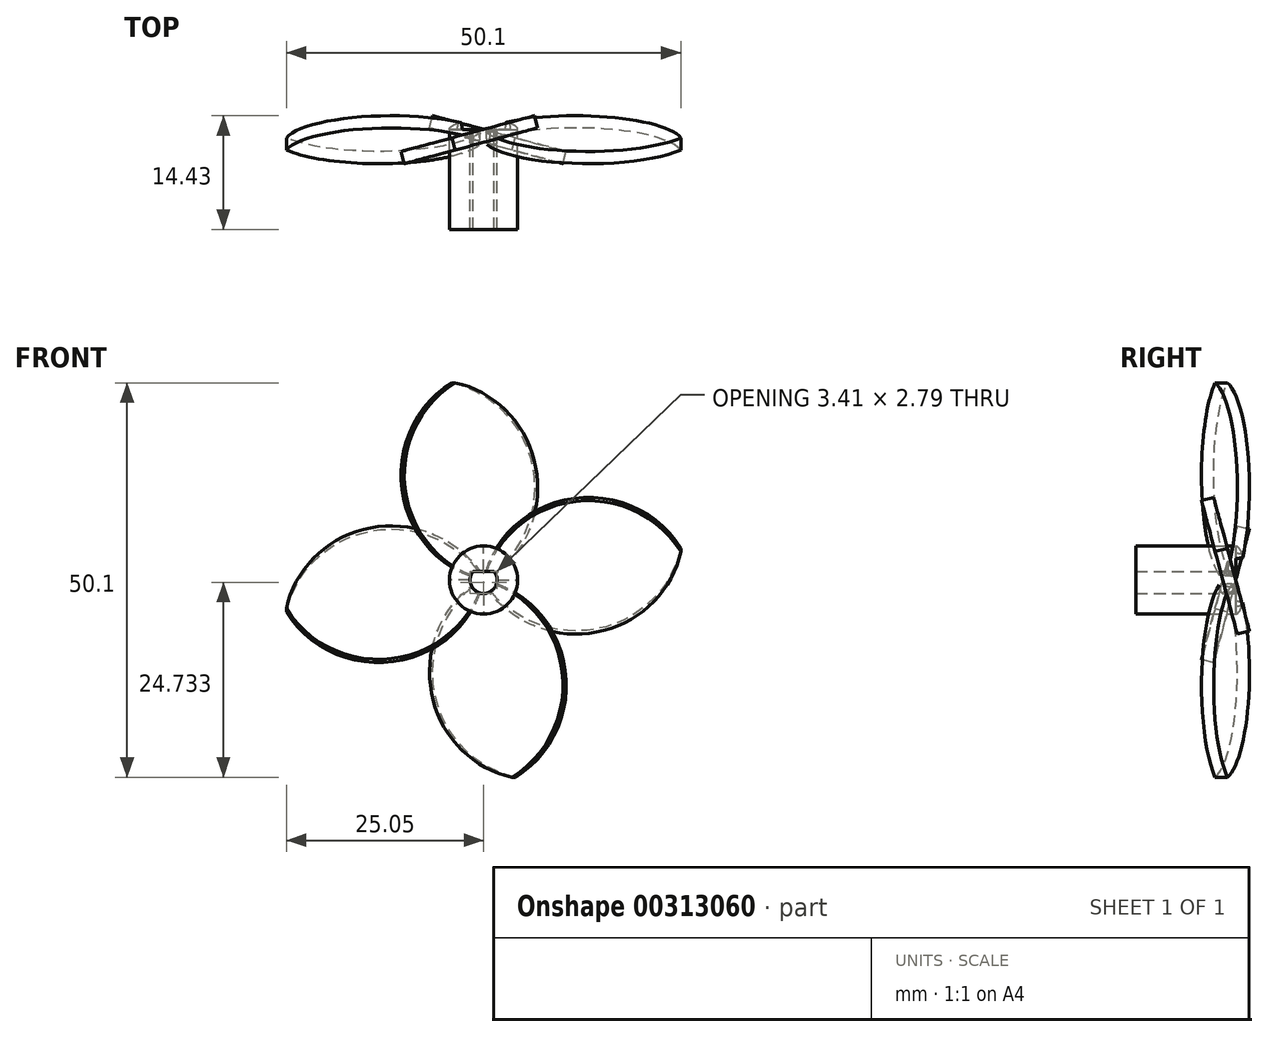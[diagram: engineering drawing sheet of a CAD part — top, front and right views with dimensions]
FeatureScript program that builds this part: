
annotation { "Feature Type Name" : "Feature", "Feature Type Description" : "" }
export const myFeature = defineFeature(function(context is Context, id is Id, definition is map)
    precondition{}
    {
        {
            var Q0;
            Q0=qCreatedBy(makeId("Front.planeOp"),FACE);
            var sketch = newSketch(context, id + "F0", { "sketchPlane" : qUnion([Q0])});
            skCircle(sketch, "E0", {"center": v(0, 0) * mm, "radius": 4.33 * mm});
            skArc(sketch, "E1", {"start": v(-1.33, 1.08) * mm, "mid": v(0, -1.71) * mm, "end": v(1.33, 1.08) * mm});
            skLineSegment(sketch, "E2", {"start": v(-1.33, 1.08) * mm, "end": v(1.33, 1.08) * mm});
            skLineSegment(sketch, "E3", {"start": v(-1.71, 0) * mm, "end": v(1.71, 0) * mm});
            skSolve(sketch);
        }
        {
            var Q0;
            Q0=makeQuery(id+"F0.imprint","IMPRINT",FACE,{"disambiguationData":[TD([[makeQuery(id+"F0.imprint","IMPRINT",EDGE,{"derivedFrom":sQuery(id+"F0.wireOp",EDGE,"E0")}),1.0]])]});
            extrude(context, id + "F1", {"entities" : qUnion([Q0]), "depth" : 12.7 * mm});
        }
        {
            var Q0;
            Q0=qCreatedBy(makeId("Front.planeOp"),FACE);
            var sketch = newSketch(context, id + "F2", { "sketchPlane" : qUnion([Q0])});
            skLineSegment(sketch, "E4", {"start": v(0, 0) * mm, "end": v(55.42, 0) * mm});
            skLineSegment(sketch, "E5", {"start": v(0, 0) * mm, "end": v(0, 53.88) * mm});
            skSolve(sketch);
        }
        {
            var Q0;
            Q0=sQuery(id+"F2.wireOp",EDGE,"E4");
            cPlane(context, id + "F3", {"entities" : qUnion([Q0]), "cplaneType" : CPlaneType.LINE_ANGLE, "offset" : 25.4 * mm, "angle" : 15 * degree, "width" : 152.4 * mm, "height" : 152.4 * mm});
        }
        {
            var Q0;
            Q0=qCreatedBy(id+"F3.planeOp",FACE);
            var sketch = newSketch(context, id + "F4", { "sketchPlane" : qUnion([Q0])});
            skLineSegment(sketch, "E6", {"start": v(0, 0) * mm, "end": v(-25.05, 4.18) * mm});
            skArc(sketch, "E7", {"start": v(-25.05, 4.18) * mm, "mid": v(-13.96, -6.5) * mm, "end": v(0, 0) * mm});
            skArc(sketch, "E8.MirrorCS", {"start": v(-25.05, 4.18) * mm, "mid": v(-11.1, 10.68) * mm, "end": v(0, 0) * mm});
            skSolve(sketch);
        }
        {
            var Q0;
            Q0 = qSketchRegion(id + "F4", true);
            extrude(context, id + "F5", {"entities" : qUnion([Q0]), "oppositeDirection" : true, "depth" : 1.6 * mm});
        }
        {
            var Q0;
            Q0=makeQuery(id+"F5.opExtrude","SWEPT_BODY",BODY,{"disambiguationData":[OSD([sQuery(id+"F4.wireOp",EDGE,"E6"),sQuery(id+"F4.wireOp",EDGE,"E7")])]});
            var Q1;
            Q1=makeQuery(id+"F1.opExtrude","SWEPT_FACE",FACE,{"disambiguationData":[OSD([sQuery(id+"F0.wireOp",EDGE,"E0")])]});
            circularPattern(context, id + "F6", {"entities" : qUnion([Q0]), "axis" : qUnion([Q1]), "angle" : 360 * degree, "instanceCount" : 4, "equalSpace" : true});
        }
        {
            var Q0;
            Q0=makeQuery(id+"F1.opExtrude","CAP_FACE",FACE,{"disambiguationData":[OSD([sQuery(id+"F0.wireOp",EDGE,"E0"),sQuery(id+"F0.wireOp",EDGE,"E1"),sQuery(id+"F0.wireOp",EDGE,"E2")])],"isStart":true});
            var sketch = newSketch(context, id + "F7", { "sketchPlane" : qUnion([Q0])});
            skSolve(sketch);
        }
        {
            var Q0;
            Q0=makeQuery(id+"F7.imprint","IMPRINT",FACE,{"disambiguationData":[TD([[makeQuery(id+"F7.imprint","IMPRINT",EDGE,{"derivedFrom":makeQuery(id+"F1.opExtrude","CAP_EDGE",EDGE,{"disambiguationData":[OSD([sQuery(id+"F0.wireOp",EDGE,"E1")])],"isStart":true})}),-1.0]])]});
            extrude(context, id + "F8", {"entities" : qUnion([Q0]), "operationType" : NewBodyOperationType.REMOVE, "oppositeDirection" : true, "depth" : 25.4 * mm});
        }
        {
            var Q0;
            Q0=makeQuery(id+"F1.opExtrude","CAP_FACE",FACE,{"disambiguationData":[OSD([sQuery(id+"F0.wireOp",EDGE,"E0"),sQuery(id+"F0.wireOp",EDGE,"E1"),sQuery(id+"F0.wireOp",EDGE,"E2")])],"isStart":true});
            extrude(context, id + "F9", {"entities" : qUnion([Q0]), "operationType" : NewBodyOperationType.REMOVE, "depth" : 25.4 * mm});
        }
        {
            var Q0;
            Q0=makeQuery(id+"F1.opExtrude","CAP_FACE",FACE,{"disambiguationData":[OSD([sQuery(id+"F0.wireOp",EDGE,"E0"),sQuery(id+"F0.wireOp",EDGE,"E1"),sQuery(id+"F0.wireOp",EDGE,"E2")])],"isStart":true});
            var sketch = newSketch(context, id + "F10", { "sketchPlane" : qUnion([Q0])});
            skSolve(sketch);
        }
        {
            var Q0;
            Q0=makeQuery(id+"F10.imprint","IMPRINT",FACE,{"disambiguationData":[TD([[makeQuery(id+"F10.imprint","IMPRINT",EDGE,{"derivedFrom":makeQuery(id+"F1.opExtrude","CAP_EDGE",EDGE,{"disambiguationData":[OSD([sQuery(id+"F0.wireOp",EDGE,"E1")])],"isStart":true})}),-1.0]])]});
            extrude(context, id + "F11", {"entities" : qUnion([Q0]), "operationType" : NewBodyOperationType.REMOVE, "depth" : 25.4 * mm});
        }
    });
